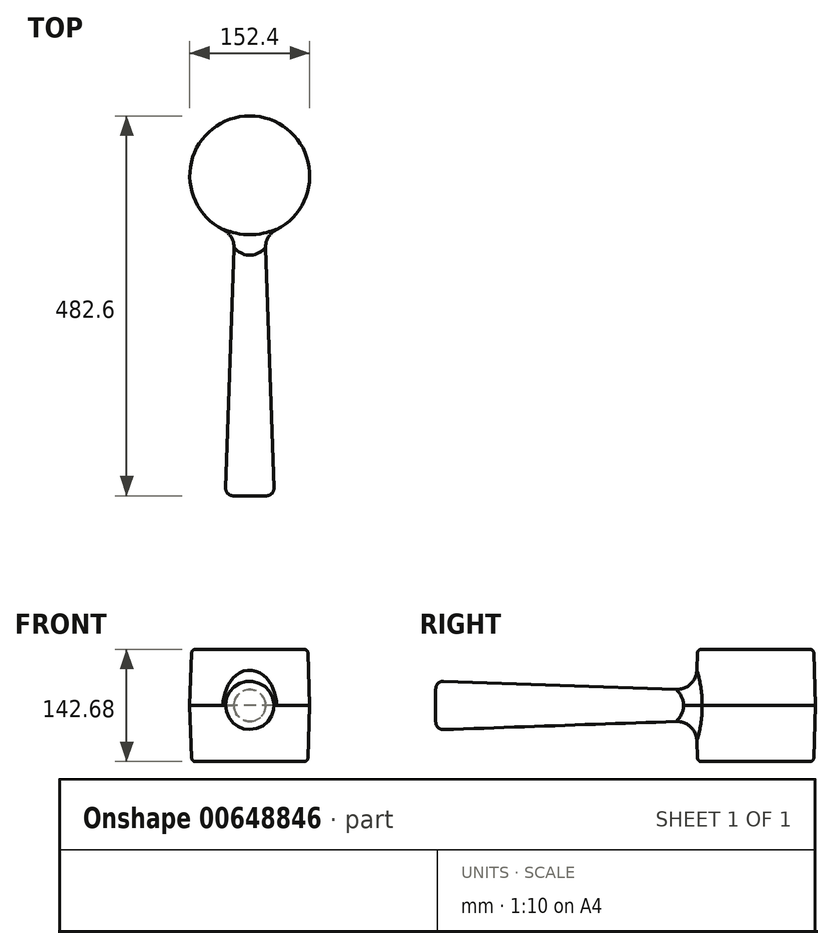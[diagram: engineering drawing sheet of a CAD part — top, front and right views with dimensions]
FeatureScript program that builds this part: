
annotation { "Feature Type Name" : "Feature", "Feature Type Description" : "" }
export const myFeature = defineFeature(function(context is Context, id is Id, definition is map)
    precondition{}
    {
        {
            var Q0;
            Q0=qCreatedBy(makeId("Top.planeOp"),FACE);
            var sketch = newSketch(context, id + "F0", { "sketchPlane" : qUnion([Q0])});
            skCircle(sketch, "E0", {"center": v(0, 0) * mm, "radius": 76.2 * mm});
            skSolve(sketch);
        }
        {
            var Q0;
            Q0=makeQuery(id+"F0.imprint","IMPRINT",FACE,{"disambiguationData":[TD([[makeQuery(id+"F0.imprint","IMPRINT",EDGE,{"derivedFrom":sQuery(id+"F0.wireOp",EDGE,"E0")}),1.0]])]});
            var Q1;
            Q1=sQuery(id+"F0.wireOp",EDGE,"E0");
            extrude(context, id + "F1", {"entities" : qUnion([Q0]), "surfaceEntities" : qUnion([Q1]), "endBound" : BoundingType.SYMMETRIC, "depth" : 142.68 * mm, "offsetDistance" : 25.4 * mm, "hasDraft" : true, "draftAngle" : 2 * degree, "draftPullDirection" : true});
        }
        {
            var Q0;
            Q0=qCreatedBy(makeId("Front.planeOp"),FACE);
            var sketch = newSketch(context, id + "F2", { "sketchPlane" : qUnion([Q0])});
            skCircle(sketch, "E1", {"center": v(0, 0) * mm, "radius": 16.83 * mm});
            skSolve(sketch);
        }
        {
            var Q0;
            Q0 = qSketchRegion(id + "F2", true);
            extrude(context, id + "F3", {"entities" : qUnion([Q0]), "operationType" : NewBodyOperationType.ADD, "depth" : 406.4 * mm, "offsetDistance" : 25.4 * mm, "hasDraft" : true, "draftAngle" : 2 * degree});
        }
        {
            var Q0;
            Q0=makeQuery(id+"F3.opExtrude","CAP_FACE",FACE,{"disambiguationData":[OSD([sQuery(id+"F2.wireOp",EDGE,"E1")])],"isStart":false});
            fillet(context, id + "F4", {"entities" : qUnion([Q0]), "radius" : 9.52 * mm, "tangentPropagation" : true, "allowEdgeOverflow" : false});
        }
        {
            var Q0;
            Q0=makeQuery(id+"F1.opExtrude","CAP_EDGE",EDGE,{"disambiguationData":[OSD([sQuery(id+"F0.wireOp",EDGE,"E0")])],"isStart":false});
            var Q1;
            Q1=makeQuery(id+"F1.opExtrude","CAP_EDGE",EDGE,{"disambiguationData":[OSD([sQuery(id+"F0.wireOp",EDGE,"E0")])],"isStart":true});
            fillet(context, id + "F5", {"entities" : qUnion([Q0, Q1]), "radius" : 5.08 * mm, "tangentPropagation" : true, "allowEdgeOverflow" : false});
        }
        {
            var Q0;
            Q0=makeQuery(id+"F3.boolean.opBoolean","INTERSECT",EDGE,{"derivedFrom":[makeQuery(id+"F1.opExtrude","SWEPT_FACE",FACE,{"disambiguationData":[OSD([sQuery(id+"F0.wireOp",EDGE,"E0")])]}),makeQuery(id+"F3.opExtrude","SWEPT_FACE",FACE,{"disambiguationData":[OSD([sQuery(id+"F2.wireOp",EDGE,"E1")])]})]});
            fillet(context, id + "F6", {"entities" : qUnion([Q0]), "radius" : 25.4 * mm, "tangentPropagation" : true, "allowEdgeOverflow" : false});
        }
    });
